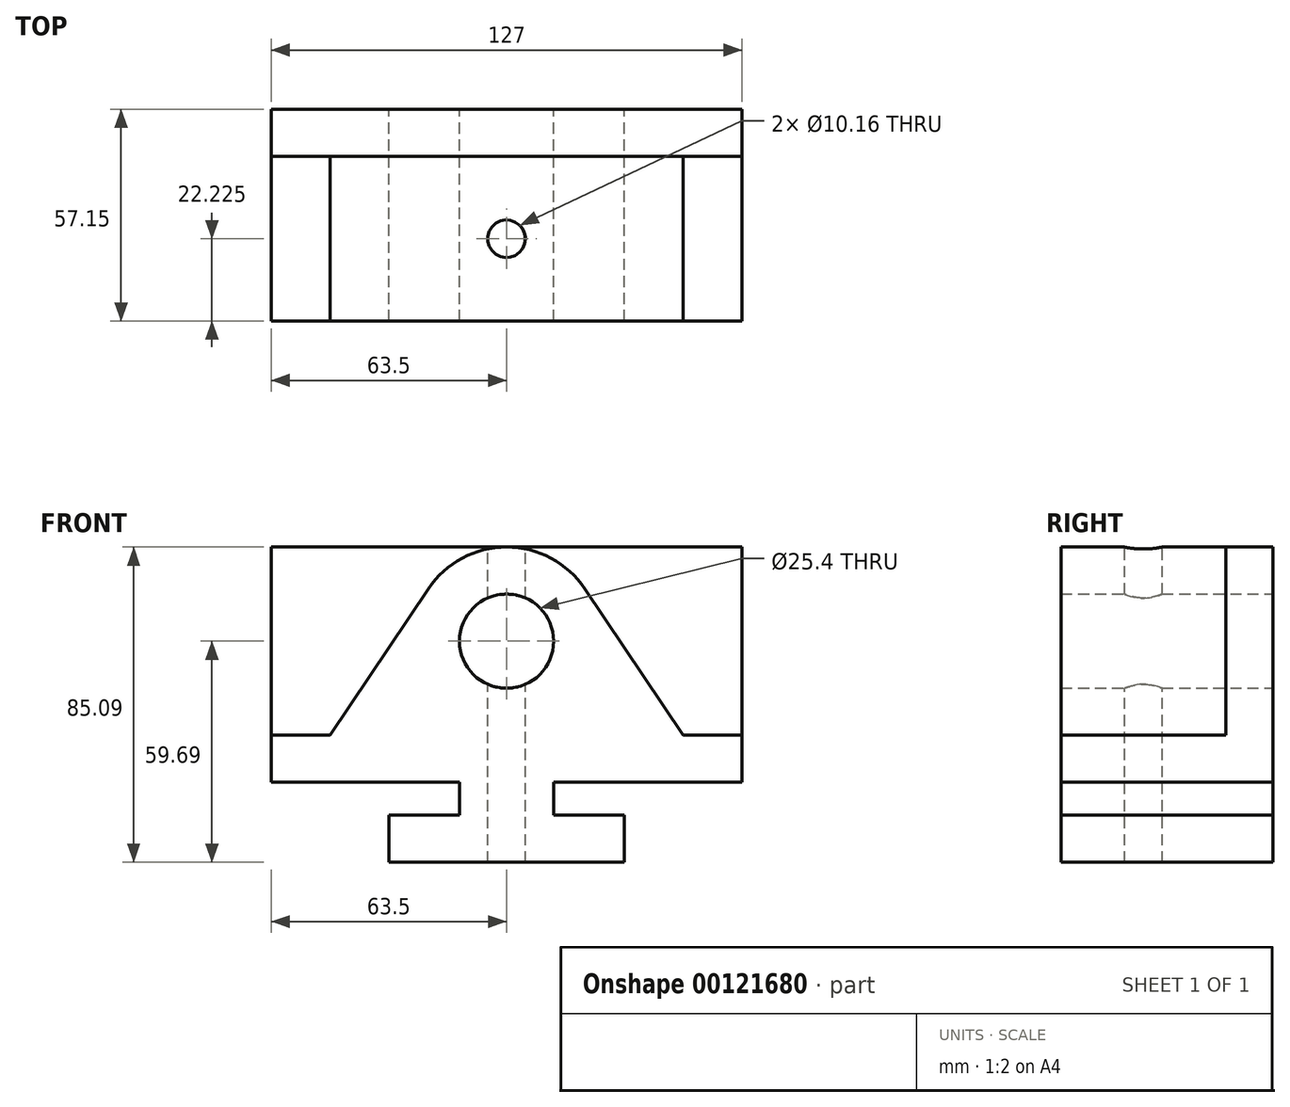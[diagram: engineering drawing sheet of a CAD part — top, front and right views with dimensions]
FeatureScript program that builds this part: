
annotation { "Feature Type Name" : "Feature", "Feature Type Description" : "" }
export const myFeature = defineFeature(function(context is Context, id is Id, definition is map)
    precondition{}
    {
        {
            var Q0;
            Q0=qCreatedBy(makeId("Front.planeOp"),FACE);
            var sketch = newSketch(context, id + "F0", { "sketchPlane" : qUnion([Q0])});
            skLineSegment(sketch, "E0", {"start": v(0, 0) * mm, "end": v(-31.75, 0) * mm});
            skLineSegment(sketch, "E1", {"start": v(-31.75, 0) * mm, "end": v(-31.75, 12.7) * mm});
            skLineSegment(sketch, "E2", {"start": v(-31.75, 12.7) * mm, "end": v(-12.7, 12.7) * mm});
            skLineSegment(sketch, "E3", {"start": v(-12.7, 12.7) * mm, "end": v(-12.7, 21.6) * mm});
            skLineSegment(sketch, "E4", {"start": v(-12.7, 21.6) * mm, "end": v(-63.5, 21.59) * mm});
            skLineSegment(sketch, "E5", {"start": v(-63.5, 21.59) * mm, "end": v(-63.5, 34.3) * mm});
            skLineSegment(sketch, "E6", {"start": v(-63.5, 34.3) * mm, "end": v(-47.63, 34.3) * mm});
            skLineSegment(sketch, "E7.MirrorCS", {"start": v(63.5, 34.3) * mm, "end": v(47.63, 34.3) * mm});
            skLineSegment(sketch, "E8.MirrorCS", {"start": v(63.5, 21.59) * mm, "end": v(63.5, 34.3) * mm});
            skLineSegment(sketch, "E9.MirrorCS", {"start": v(12.7, 21.6) * mm, "end": v(63.5, 21.6) * mm});
            skLineSegment(sketch, "E10.MirrorCS", {"start": v(12.7, 12.7) * mm, "end": v(12.7, 21.6) * mm});
            skLineSegment(sketch, "E11.MirrorCS", {"start": v(31.75, 12.7) * mm, "end": v(12.7, 12.7) * mm});
            skLineSegment(sketch, "E12.MirrorCS", {"start": v(31.75, 0) * mm, "end": v(31.75, 12.7) * mm});
            skLineSegment(sketch, "E13.MirrorCS", {"start": v(0, 0) * mm, "end": v(31.75, 0) * mm});
            skLineSegment(sketch, "E14", {"start": v(-63.5, 34.3) * mm, "end": v(-63.5, 85.1) * mm});
            skLineSegment(sketch, "E15", {"start": v(-63.5, 85.1) * mm, "end": v(63.5, 85.1) * mm});
            skLineSegment(sketch, "E16", {"start": v(63.5, 85.1) * mm, "end": v(63.5, 34.3) * mm});
            skCircle(sketch, "E17", {"center": v(0, 59.69) * mm, "radius": 12.7 * mm});
            skArc(sketch, "E18", {"start": v(21.1, 73.84) * mm, "mid": v(0, 85.1) * mm, "end": v(-21.1, 73.84) * mm});
            skLineSegment(sketch, "E19", {"start": v(-47.63, 34.3) * mm, "end": v(-21.1, 73.84) * mm});
            skLineSegment(sketch, "E20", {"start": v(47.63, 34.3) * mm, "end": v(21.1, 73.84) * mm});
            skSolve(sketch);
        }
        {
            var Q0;
            Q0=makeQuery(id+"F0.imprint","IMPRINT",FACE,{"disambiguationData":[TD([[makeQuery(id+"F0.imprint","IMPRINT",EDGE,{"derivedFrom":sQuery(id+"F0.wireOp",EDGE,"E0")}),-1.0]])]});
            extrude(context, id + "F1", {"entities" : qUnion([Q0]), "depth" : 44.45 * mm});
        }
        {
            var Q0;
            Q0=makeQuery(id+"F0.imprint","IMPRINT",FACE,{"disambiguationData":[TD([[makeQuery(id+"F0.imprint","IMPRINT",EDGE,{"derivedFrom":sQuery(id+"F0.wireOp",EDGE,"E6")}),1.0]])]});
            var Q1;
            Q1=makeQuery(id+"F0.imprint","IMPRINT",FACE,{"disambiguationData":[TD([[makeQuery(id+"F0.imprint","IMPRINT",EDGE,{"derivedFrom":sQuery(id+"F0.wireOp",EDGE,"E7.MirrorCS")}),-1.0]])]});
            var Q2;
            Q2=makeQuery(id+"F0.imprint","IMPRINT",FACE,{"disambiguationData":[TD([[makeQuery(id+"F0.imprint","IMPRINT",EDGE,{"derivedFrom":sQuery(id+"F0.wireOp",EDGE,"E0")}),-1.0]])]});
            extrude(context, id + "F2", {"entities" : qUnion([Q0, Q1, Q2]), "operationType" : NewBodyOperationType.ADD, "oppositeDirection" : true, "depth" : 12.7 * mm});
        }
        {
            var Q0;
            Q0=makeQuery(id+"F2.opExtrude","SWEPT_FACE",FACE,{"disambiguationData":[OSD([sQuery(id+"F0.wireOp",EDGE,"E15")])]});
            var sketch = newSketch(context, id + "F3", { "sketchPlane" : qUnion([Q0])});
            skCircle(sketch, "E21", {"center": v(0, -22.23) * mm, "radius": 5.08 * mm});
            skSolve(sketch);
        }
        {
            var Q0;
            Q0=makeQuery(id+"F3.imprint","IMPRINT",FACE,{"disambiguationData":[TD([[makeQuery(id+"F3.imprint","IMPRINT",EDGE,{"derivedFrom":sQuery(id+"F3.wireOp",EDGE,"E21")}),1.0]])]});
            extrude(context, id + "F4", {"entities" : qUnion([Q0]), "operationType" : NewBodyOperationType.REMOVE, "endBound" : BoundingType.THROUGH_ALL, "oppositeDirection" : true, "depth" : 25.4 * mm});
        }
    });
